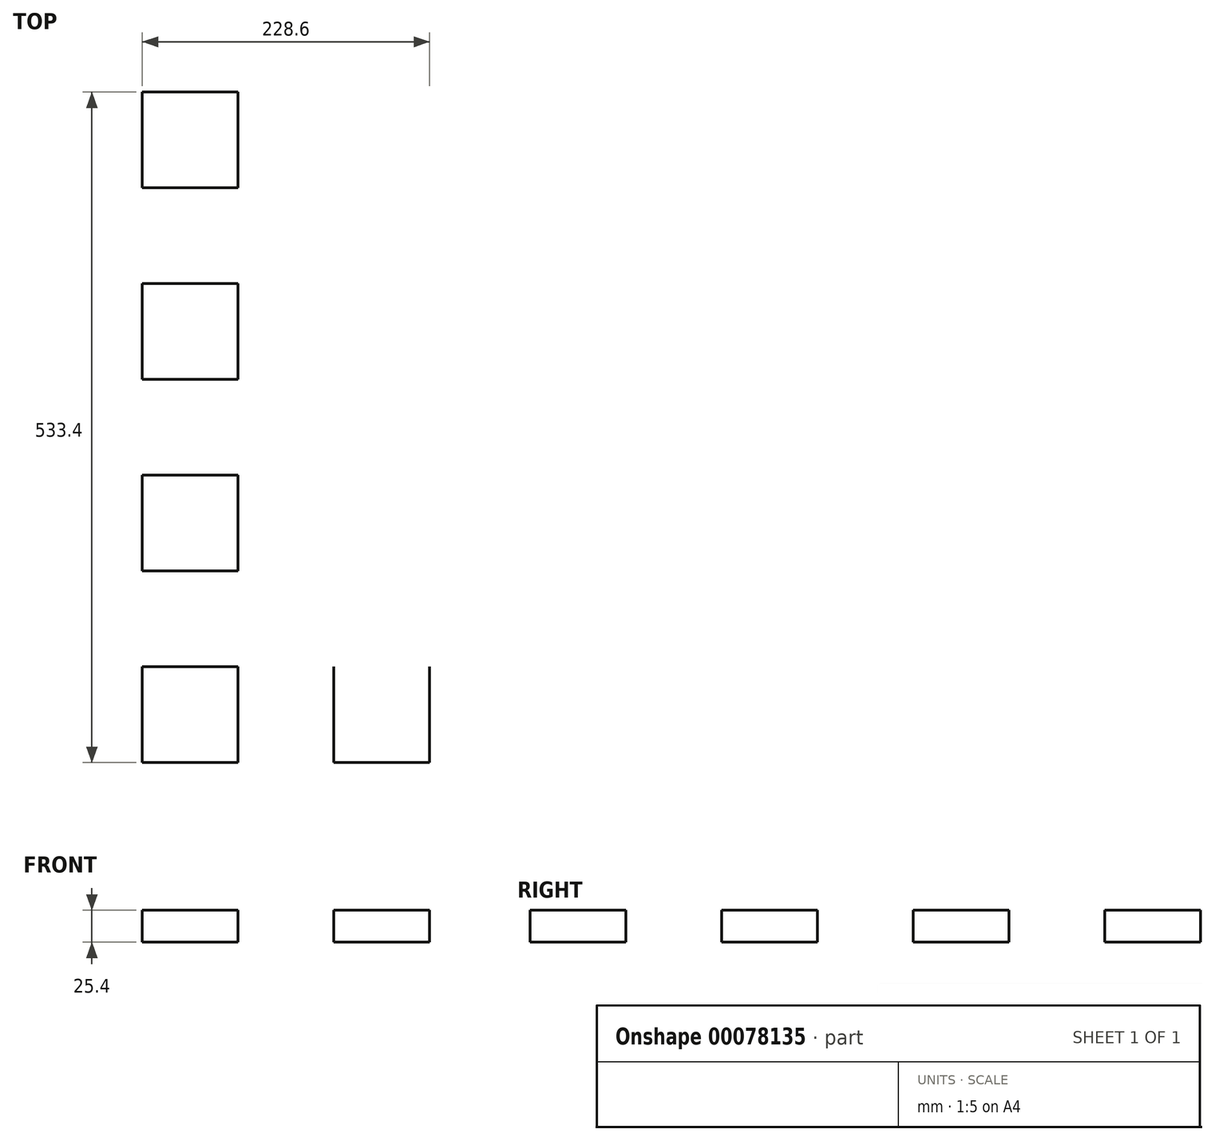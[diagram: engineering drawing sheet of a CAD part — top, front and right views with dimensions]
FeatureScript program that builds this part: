
annotation { "Feature Type Name" : "Feature", "Feature Type Description" : "" }
export const myFeature = defineFeature(function(context is Context, id is Id, definition is map)
    precondition{}
    {
        {
            var Q0;
            Q0=qCreatedBy(makeId("Top.planeOp"),FACE);
            var sketch = newSketch(context, id + "F0", { "sketchPlane" : qUnion([Q0])});
            skLineSegment(sketch, "E0.bottom", {"start": v(-1271.73, 494.46) * mm, "end": v(1268.27, 494.46) * mm});
            skLineSegment(sketch, "E0.top", {"start": v(-1271.73, -775.54) * mm, "end": v(1268.27, -775.54) * mm});
            skLineSegment(sketch, "E0.left", {"start": v(-1271.73, 494.46) * mm, "end": v(-1271.73, -775.54) * mm});
            skLineSegment(sketch, "E0.right", {"start": v(1268.27, 494.46) * mm, "end": v(1268.27, -775.54) * mm});
            skLineSegment(sketch, "E1.bottom", {"start": v(-1195.53, -623.14) * mm, "end": v(-1119.33, -623.14) * mm});
            skLineSegment(sketch, "E1.top", {"start": v(-1195.53, -699.34) * mm, "end": v(-1119.33, -699.34) * mm});
            skLineSegment(sketch, "E1.left", {"start": v(-1195.53, -623.14) * mm, "end": v(-1195.53, -699.34) * mm});
            skLineSegment(sketch, "E1.right", {"start": v(-1119.33, -623.14) * mm, "end": v(-1119.33, -699.34) * mm});
            skLineSegment(sketch, "E2.1.0.0", {"start": v(-966.93, -623.14) * mm, "end": v(-966.93, -699.34) * mm});
            skLineSegment(sketch, "E2.1.0.1", {"start": v(-1043.13, -623.14) * mm, "end": v(-966.93, -623.14) * mm});
            skLineSegment(sketch, "E2.1.0.2", {"start": v(-1043.13, -623.14) * mm, "end": v(-1043.13, -699.34) * mm});
            skLineSegment(sketch, "E2.1.0.3", {"start": v(-1043.13, -699.34) * mm, "end": v(-966.93, -699.34) * mm});
            skLineSegment(sketch, "E2.2.0.0", {"start": v(-814.53, -623.14) * mm, "end": v(-814.53, -699.34) * mm});
            skLineSegment(sketch, "E2.2.0.1", {"start": v(-890.73, -623.14) * mm, "end": v(-814.53, -623.14) * mm});
            skLineSegment(sketch, "E2.2.0.2", {"start": v(-890.73, -623.14) * mm, "end": v(-890.73, -699.34) * mm});
            skLineSegment(sketch, "E2.2.0.3", {"start": v(-890.73, -699.34) * mm, "end": v(-814.53, -699.34) * mm});
            skLineSegment(sketch, "E2.3.0.0", {"start": v(-662.13, -623.14) * mm, "end": v(-662.13, -699.34) * mm});
            skLineSegment(sketch, "E2.3.0.1", {"start": v(-738.33, -623.14) * mm, "end": v(-662.13, -623.14) * mm});
            skLineSegment(sketch, "E2.3.0.2", {"start": v(-738.33, -623.14) * mm, "end": v(-738.33, -699.34) * mm});
            skLineSegment(sketch, "E2.3.0.3", {"start": v(-738.33, -699.34) * mm, "end": v(-662.13, -699.34) * mm});
            skLineSegment(sketch, "E2.direction1", {"start": v(-890.73, -648.54) * mm, "end": v(-738.33, -648.54) * mm, "construction": true});
            skLineSegment(sketch, "E3.0.1.0", {"start": v(-1119.33, -470.74) * mm, "end": v(-1119.33, -546.94) * mm});
            skLineSegment(sketch, "E3.0.1.1", {"start": v(-1195.53, -470.74) * mm, "end": v(-1119.33, -470.74) * mm});
            skLineSegment(sketch, "E3.0.1.2", {"start": v(-1195.53, -470.74) * mm, "end": v(-1195.53, -546.94) * mm});
            skLineSegment(sketch, "E3.0.1.3", {"start": v(-1195.53, -546.94) * mm, "end": v(-1119.33, -546.94) * mm});
            skLineSegment(sketch, "E3.0.2.0", {"start": v(-1119.33, -318.34) * mm, "end": v(-1119.33, -394.54) * mm});
            skLineSegment(sketch, "E3.0.2.1", {"start": v(-1195.53, -318.34) * mm, "end": v(-1119.33, -318.34) * mm});
            skLineSegment(sketch, "E3.0.2.2", {"start": v(-1195.53, -318.34) * mm, "end": v(-1195.53, -394.54) * mm});
            skLineSegment(sketch, "E3.0.2.3", {"start": v(-1195.53, -394.54) * mm, "end": v(-1119.33, -394.54) * mm});
            skLineSegment(sketch, "E3.direction1", {"start": v(-1119.33, -699.34) * mm, "end": v(-1093.93, -699.34) * mm, "construction": true});
            skLineSegment(sketch, "E3.direction2", {"start": v(-1119.33, -699.34) * mm, "end": v(-1119.33, -546.94) * mm, "construction": true});
            skLineSegment(sketch, "E4.0.0.3", {"start": v(-1119.33, -165.94) * mm, "end": v(-1119.33, -242.14) * mm});
            skLineSegment(sketch, "E4.3.0.3", {"start": v(-1195.53, -165.94) * mm, "end": v(-1119.33, -165.94) * mm});
            skLineSegment(sketch, "E4.6.0.3", {"start": v(-1195.53, -165.94) * mm, "end": v(-1195.53, -242.14) * mm});
            skLineSegment(sketch, "E4.9.0.3", {"start": v(-1195.53, -242.14) * mm, "end": v(-1119.33, -242.14) * mm});
            skLineSegment(sketch, "E5.0.4.0", {"start": v(-509.73, -623.14) * mm, "end": v(-509.73, -699.34) * mm});
            skLineSegment(sketch, "E5.3.4.0", {"start": v(-585.93, -623.14) * mm, "end": v(-509.73, -623.14) * mm});
            skLineSegment(sketch, "E5.6.4.0", {"start": v(-585.93, -623.14) * mm, "end": v(-585.93, -699.34) * mm});
            skLineSegment(sketch, "E5.9.4.0", {"start": v(-585.93, -699.34) * mm, "end": v(-509.73, -699.34) * mm});
            skLineSegment(sketch, "E5.0.5.0", {"start": v(-357.33, -623.14) * mm, "end": v(-357.33, -699.34) * mm});
            skLineSegment(sketch, "E5.3.5.0", {"start": v(-433.53, -623.14) * mm, "end": v(-357.33, -623.14) * mm});
            skLineSegment(sketch, "E5.6.5.0", {"start": v(-433.53, -623.14) * mm, "end": v(-433.53, -699.34) * mm});
            skLineSegment(sketch, "E5.9.5.0", {"start": v(-433.53, -699.34) * mm, "end": v(-357.33, -699.34) * mm});
            skLineSegment(sketch, "E6", {"start": v(-433.53, -242.14) * mm, "end": v(-357.33, -242.14) * mm});
            skLineSegment(sketch, "E7", {"start": v(-357.33, -242.14) * mm, "end": v(-357.33, -165.94) * mm});
            skLineSegment(sketch, "E8", {"start": v(-357.33, -165.94) * mm, "end": v(-433.53, -165.94) * mm});
            skLineSegment(sketch, "E9", {"start": v(-433.53, -165.94) * mm, "end": v(-433.53, -242.14) * mm});
            skSolve(sketch);
        }
        {
            var Q0;
            Q0=sQuery(id+"F0.wireOp",EDGE,"E4.9.0.3");
            var Q1;
            Q1=sQuery(id+"F0.wireOp",EDGE,"E4.0.0.3");
            var Q2;
            Q2=sQuery(id+"F0.wireOp",EDGE,"E4.3.0.3");
            var Q3;
            Q3=sQuery(id+"F0.wireOp",EDGE,"E4.6.0.3");
            var Q4;
            Q4=sQuery(id+"F0.wireOp",EDGE,"E3.0.2.1");
            var Q5;
            Q5=sQuery(id+"F0.wireOp",EDGE,"E3.0.2.0");
            var Q6;
            Q6=sQuery(id+"F0.wireOp",EDGE,"E3.0.2.2");
            var Q7;
            Q7=sQuery(id+"F0.wireOp",EDGE,"E3.0.1.0");
            var Q8;
            Q8=sQuery(id+"F0.wireOp",EDGE,"E3.0.1.1");
            var Q9;
            Q9=sQuery(id+"F0.wireOp",EDGE,"E3.0.2.3");
            var Q10;
            Q10=sQuery(id+"F0.wireOp",EDGE,"E3.0.1.2");
            var Q11;
            Q11=sQuery(id+"F0.wireOp",EDGE,"E3.0.1.3");
            var Q12;
            Q12=sQuery(id+"F0.wireOp",EDGE,"E1.bottom");
            var Q13;
            Q13=sQuery(id+"F0.wireOp",EDGE,"E1.right");
            var Q14;
            Q14=sQuery(id+"F0.wireOp",EDGE,"E1.left");
            var Q15;
            Q15=sQuery(id+"F0.wireOp",EDGE,"E1.top");
            var Q16;
            Q16=sQuery(id+"F0.wireOp",EDGE,"E2.1.0.3");
            var Q17;
            Q17=sQuery(id+"F0.wireOp",EDGE,"E2.1.0.2");
            var Q18;
            Q18=sQuery(id+"F0.wireOp",EDGE,"E2.1.0.0");
            extrude(context, id + "F1", {"bodyType" : ToolBodyType.SURFACE, "surfaceEntities" : qUnion([Q0, Q1, Q2, Q3, Q4, Q5, Q6, Q7, Q8, Q9, Q10, Q11, Q12, Q13, Q14, Q15, Q16, Q17, Q18]), "depth" : 25.4 * mm});
        }
    });
